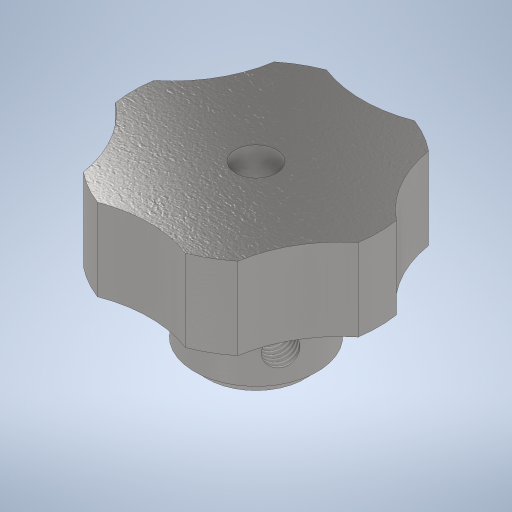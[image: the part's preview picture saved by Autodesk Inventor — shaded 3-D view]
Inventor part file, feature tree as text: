
AUTODESK INVENTOR PART (.ipt)
format: ipt  version: 2024 (Build 280153000, 153)  size: 354,816 bytes
history: native  units: mm
features: extrude x5, sketch x4, thread x2, pattern_circular x1, chamfer x1, plane x1
ambient origin geometry x8: Origin, YZ Plane, XZ Plane, XY Plane, X Axis, Y Axis, Z Axis, Center Point
bodies: Volumenkörper1 (feature_tree)
feature tree (14):
  sketch  "Skizze1"  dims[d0=30.0mm d1=15.0mm]
  extrude  "Extrusion1"  Depth=15.0mm
  extrude  "Extrusion2"  Depth=10.0mm TaperAngle=0.0deg
  pattern_circular  "Runde Anordnung1"  Count=6 Angle=360.0deg
  extrude  "Extrusion3"  Depth=10.0mm TaperAngle=0.0deg
  chamfer  "Fasen1"  Distance=1.5mm Angle=45.0deg
  extrude  "Extrusion4"  Depth=10.0mm
  plane  "Arbeitsebene2"
  extrude  "Extrusion5"  Depth=10.0mm TaperAngle=0.0deg
  thread  "Gewinde2"  [1 undecoded]
  thread  "Gewinde3"  [1 undecoded]
  sketch  "Skizze2"  dims[d2=13.0mm d3=10.0mm d4=0.0mm]
  sketch  "Skizze3"  dims[d5=10.0mm d6=0.0mm d7=60.0mm d8=360.0deg]
  sketch  "Skizze5"  dims[d10=15.0mm d11=10.0mm d12=0.0mm d13=1.5mm d14=2.0mm d15=45.0deg d16=5.0mm d17=10.0mm d18=0.0mm d21=3.5mm d22=5.0mm d23=10.0mm d24=0.0mm d27=25.0mm d28=0.0mm d29=25.0mm d30=0.0mm d25=0.25mm d26=0.375mm d31=0.75mm d32=0.375mm]
note: 2 required parameter values undecoded (feature->parameter linkage not recoverable at this tier; creation-order binding heuristic only, values carry confidence <= 0.55)
